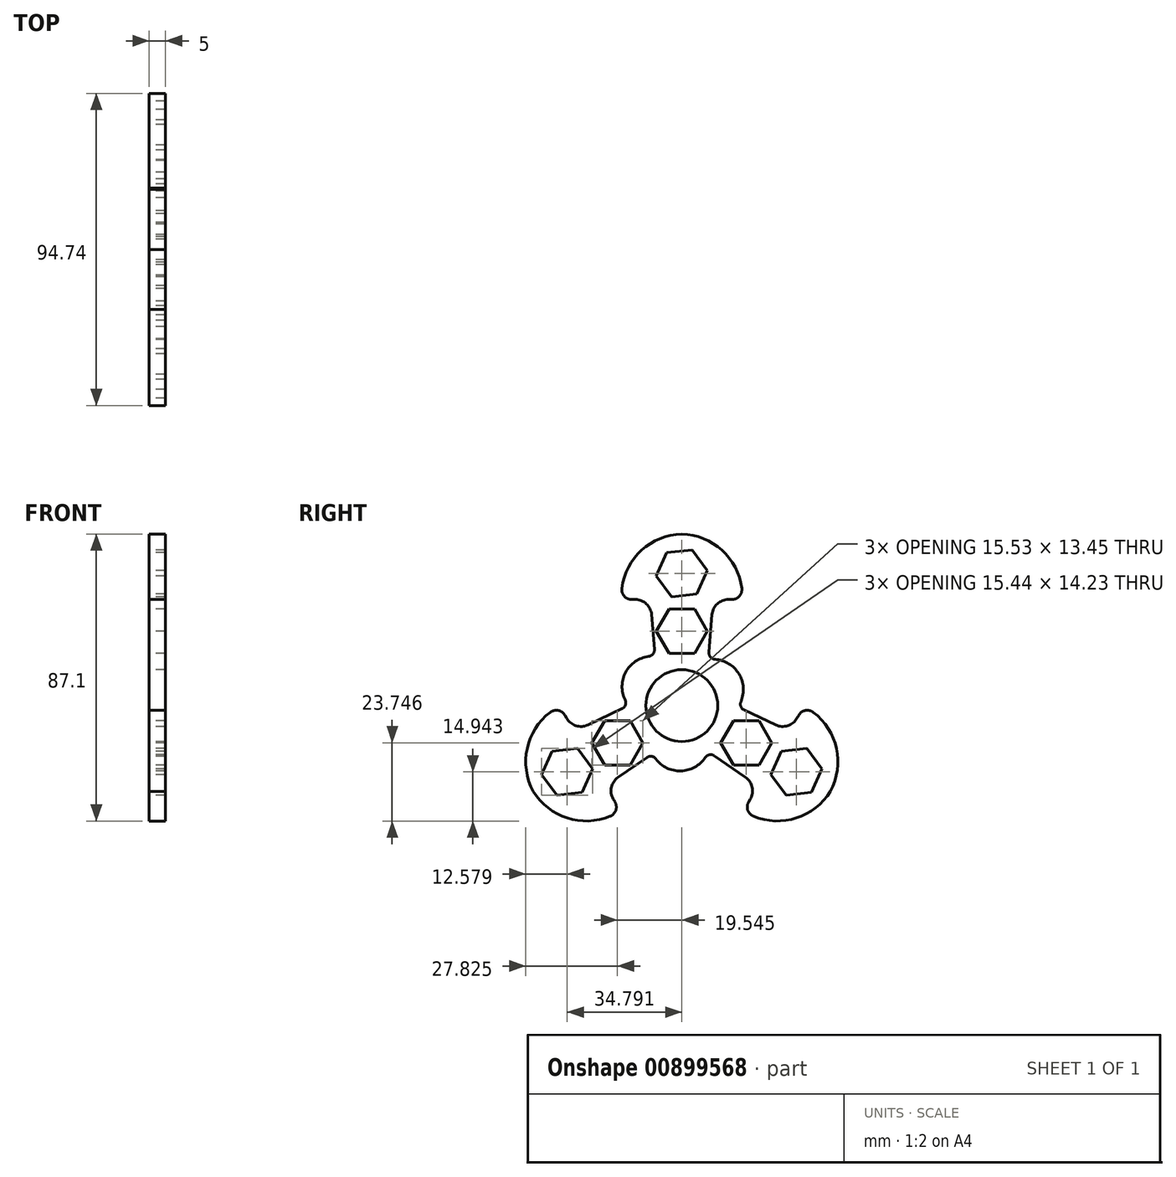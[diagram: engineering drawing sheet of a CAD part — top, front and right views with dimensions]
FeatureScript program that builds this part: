
annotation { "Feature Type Name" : "Feature", "Feature Type Description" : "" }
export const myFeature = defineFeature(function(context is Context, id is Id, definition is map)
    precondition{}
    {
        {
            var Q0;
            Q0=qCreatedBy(makeId("Right.planeOp"),FACE);
            var sketch = newSketch(context, id + "F0", { "sketchPlane" : qUnion([Q0])});
            skCircle(sketch, "E0", {"center": v(0, 0) * mm, "radius": 10.9 * mm});
            skCircle(sketch, "E1.cCircle", {"center": v(0, 22.57) * mm, "radius": 6.72 * mm, "construction": true});
            skLineSegment(sketch, "E1.0", {"start": v(-3.88, 29.3) * mm, "end": v(3.88, 29.3) * mm});
            skLineSegment(sketch, "E1.1", {"start": v(3.88, 29.3) * mm, "end": v(7.77, 22.57) * mm});
            skLineSegment(sketch, "E1.2", {"start": v(7.77, 22.57) * mm, "end": v(3.88, 15.84) * mm});
            skLineSegment(sketch, "E1.3", {"start": v(3.88, 15.84) * mm, "end": v(-3.88, 15.84) * mm});
            skLineSegment(sketch, "E1.4", {"start": v(-3.88, 15.84) * mm, "end": v(-7.77, 22.57) * mm});
            skLineSegment(sketch, "E1.5", {"start": v(-7.77, 22.57) * mm, "end": v(-3.88, 29.3) * mm});
            skPoint(sketch, "E1.0.midPoint", {"position": v(0, 29.3) * mm});
            skCircle(sketch, "E2.cCircle", {"center": v(0, 40.17) * mm, "radius": 6.72 * mm, "construction": true});
            skLineSegment(sketch, "E2.0", {"start": v(-7.72, 39.32) * mm, "end": v(-4.6, 46.43) * mm});
            skLineSegment(sketch, "E2.1", {"start": v(-4.6, 46.43) * mm, "end": v(3.12, 47.29) * mm});
            skLineSegment(sketch, "E2.2", {"start": v(3.12, 47.29) * mm, "end": v(7.72, 41.03) * mm});
            skLineSegment(sketch, "E2.3", {"start": v(7.72, 41.03) * mm, "end": v(4.6, 33.92) * mm});
            skLineSegment(sketch, "E2.4", {"start": v(4.6, 33.92) * mm, "end": v(-3.12, 33.06) * mm});
            skLineSegment(sketch, "E2.5", {"start": v(-3.12, 33.06) * mm, "end": v(-7.72, 39.32) * mm});
            skPoint(sketch, "E2.0.midPoint", {"position": v(-6.16, 42.87) * mm});
            skLineSegment(sketch, "E3", {"start": v(-8.3, 17.07) * mm, "end": v(-9.17, 27.6) * mm});
            skLineSegment(sketch, "E4.MirrorCS", {"start": v(8.24, 16.2) * mm, "end": v(9.17, 27.6) * mm});
            skLineSegment(sketch, "E5.1.0", {"start": v(-37.9, -27.2) * mm, "end": v(-42.5, -20.94) * mm});
            skLineSegment(sketch, "E5.1.1", {"start": v(-42.5, -20.94) * mm, "end": v(-39.4, -13.83) * mm});
            skLineSegment(sketch, "E5.1.2", {"start": v(-39.4, -13.83) * mm, "end": v(-31.68, -12.97) * mm});
            skCircle(sketch, "E5.1.3", {"center": v(-34.8, -20.09) * mm, "radius": 6.72 * mm, "construction": true});
            skLineSegment(sketch, "E5.1.4", {"start": v(-31.68, -12.97) * mm, "end": v(-27.07, -19.23) * mm});
            skLineSegment(sketch, "E5.1.5", {"start": v(-27.07, -19.23) * mm, "end": v(-30.19, -26.34) * mm});
            skLineSegment(sketch, "E5.1.6", {"start": v(-30.19, -26.34) * mm, "end": v(-37.9, -27.2) * mm});
            skLineSegment(sketch, "E5.1.7", {"start": v(-10.63, -15.73) * mm, "end": v(-19.32, -21.74) * mm});
            skLineSegment(sketch, "E5.1.10", {"start": v(-18.14, -0.96) * mm, "end": v(-28.5, -5.86) * mm});
            skLineSegment(sketch, "E5.1.11", {"start": v(-27.31, -11.28) * mm, "end": v(-23.43, -4.56) * mm});
            skCircle(sketch, "E5.1.12", {"center": v(-19.54, -11.28) * mm, "radius": 6.72 * mm, "construction": true});
            skLineSegment(sketch, "E5.1.13", {"start": v(-23.43, -4.56) * mm, "end": v(-15.66, -4.56) * mm});
            skLineSegment(sketch, "E5.1.14", {"start": v(-15.66, -4.56) * mm, "end": v(-11.78, -11.28) * mm});
            skLineSegment(sketch, "E5.1.15", {"start": v(-11.78, -11.28) * mm, "end": v(-15.66, -18) * mm});
            skLineSegment(sketch, "E5.1.16", {"start": v(-15.66, -18) * mm, "end": v(-23.43, -18) * mm});
            skLineSegment(sketch, "E5.1.17", {"start": v(-23.43, -18) * mm, "end": v(-27.31, -11.28) * mm});
            skLineSegment(sketch, "E5.2.0", {"start": v(42.5, -19.23) * mm, "end": v(39.4, -26.34) * mm});
            skLineSegment(sketch, "E5.2.1", {"start": v(39.4, -26.34) * mm, "end": v(31.68, -27.2) * mm});
            skLineSegment(sketch, "E5.2.2", {"start": v(31.68, -27.2) * mm, "end": v(27.07, -20.94) * mm});
            skCircle(sketch, "E5.2.3", {"center": v(34.8, -20.09) * mm, "radius": 6.72 * mm, "construction": true});
            skLineSegment(sketch, "E5.2.4", {"start": v(27.07, -20.94) * mm, "end": v(30.19, -13.83) * mm});
            skLineSegment(sketch, "E5.2.5", {"start": v(30.19, -13.83) * mm, "end": v(37.9, -12.97) * mm});
            skLineSegment(sketch, "E5.2.6", {"start": v(37.9, -12.97) * mm, "end": v(42.5, -19.23) * mm});
            skLineSegment(sketch, "E5.2.7", {"start": v(18.93, -1.34) * mm, "end": v(28.5, -5.86) * mm});
            skLineSegment(sketch, "E5.2.10", {"start": v(9.9, -15.23) * mm, "end": v(19.32, -21.74) * mm});
            skLineSegment(sketch, "E5.2.11", {"start": v(23.43, -18) * mm, "end": v(15.66, -18) * mm});
            skCircle(sketch, "E5.2.12", {"center": v(19.54, -11.28) * mm, "radius": 6.72 * mm, "construction": true});
            skLineSegment(sketch, "E5.2.13", {"start": v(15.66, -18) * mm, "end": v(11.78, -11.28) * mm});
            skLineSegment(sketch, "E5.2.14", {"start": v(11.78, -11.28) * mm, "end": v(15.66, -4.56) * mm});
            skLineSegment(sketch, "E5.2.15", {"start": v(15.66, -4.56) * mm, "end": v(23.43, -4.56) * mm});
            skLineSegment(sketch, "E5.2.16", {"start": v(23.43, -4.56) * mm, "end": v(27.31, -11.28) * mm});
            skLineSegment(sketch, "E5.2.17", {"start": v(27.31, -11.28) * mm, "end": v(23.43, -18) * mm});
            skLineSegment(sketch, "E6", {"start": v(-14.15, 32.2) * mm, "end": v(-15.23, 32.2) * mm});
            skArc(sketch, "E7", {"start": v(0, 52.07) * mm, "mid": v(-12.15, 47.19) * mm, "end": v(-18.2, 35.57) * mm});
            skArc(sketch, "E8.MirrorCS", {"start": v(0, 52.07) * mm, "mid": v(12.15, 47.19) * mm, "end": v(18.2, 35.57) * mm});
            skLineSegment(sketch, "E9.MirrorCS", {"start": v(14.15, 32.2) * mm, "end": v(15.23, 32.2) * mm});
            skLineSegment(sketch, "E10.1.0", {"start": v(-20.8, -28.35) * mm, "end": v(-20.27, -29.29) * mm});
            skArc(sketch, "E10.1.1", {"start": v(-45.1, -26.03) * mm, "mid": v(-34.79, -34.12) * mm, "end": v(-21.7, -33.55) * mm});
            skArc(sketch, "E10.1.2", {"start": v(-45.1, -26.03) * mm, "mid": v(-46.94, -13.07) * mm, "end": v(-39.91, -2.02) * mm});
            skLineSegment(sketch, "E10.1.3", {"start": v(-34.96, -3.84) * mm, "end": v(-35.5, -2.9) * mm});
            skLineSegment(sketch, "E10.2.0", {"start": v(34.96, -3.84) * mm, "end": v(35.5, -2.9) * mm});
            skArc(sketch, "E10.2.1", {"start": v(45.1, -26.03) * mm, "mid": v(46.94, -13.07) * mm, "end": v(39.91, -2.02) * mm});
            skArc(sketch, "E10.2.2", {"start": v(45.1, -26.03) * mm, "mid": v(34.79, -34.12) * mm, "end": v(21.7, -33.55) * mm});
            skLineSegment(sketch, "E10.2.3", {"start": v(20.8, -28.35) * mm, "end": v(20.27, -29.29) * mm});
            skArc(sketch, "E11", {"start": v(-10.06, 14.92) * mm, "mid": v(-17.03, 10.16) * mm, "end": v(-17.2, 1.72) * mm});
            skArc(sketch, "E12.1.0", {"start": v(-7.9, -16.17) * mm, "mid": v(-0.29, -19.83) * mm, "end": v(7.1, -15.76) * mm});
            skArc(sketch, "E12.2.0", {"start": v(17.95, 1.25) * mm, "mid": v(17.31, 9.67) * mm, "end": v(10.1, 14.03) * mm});
            skPoint(sketch, "E13.orphan", {"position": v(-7.55, 7.86) * mm});
            skPoint(sketch, "E14.visualSharp", {"position": v(-32.66, -7.83) * mm});
            skArc(sketch, "E14.filletArc", {"start": v(-34.96, -3.84) * mm, "mid": v(-32.12, -6.12) * mm, "end": v(-28.5, -5.86) * mm});
            skLineSegment(sketch, "E15.bottom", {"start": v(-55.43, 26.12) * mm, "end": v(-55.58, 26.12) * mm});
            skLineSegment(sketch, "E15.top", {"start": v(-55.43, 24.8) * mm, "end": v(-55.58, 24.8) * mm});
            skLineSegment(sketch, "E15.left", {"start": v(-55.43, 26.12) * mm, "end": v(-55.43, 24.8) * mm});
            skLineSegment(sketch, "E15.right", {"start": v(-55.58, 26.12) * mm, "end": v(-55.58, 24.8) * mm});
            skLineSegment(sketch, "E16.bottom", {"start": v(-68.95, 33.26) * mm, "end": v(-42.65, 33.26) * mm});
            skLineSegment(sketch, "E16.top", {"start": v(-67.95, 2.56) * mm, "end": v(-47.15, 2.56) * mm});
            skLineSegment(sketch, "E16.left", {"start": v(-70.95, 31.26) * mm, "end": v(-70.95, 5.56) * mm});
            skLineSegment(sketch, "E16.right", {"start": v(-42.15, 32.76) * mm, "end": v(-42.15, 7.56) * mm});
            skPoint(sketch, "E17.visualSharp", {"position": v(-42.15, 33.26) * mm});
            skArc(sketch, "E17.filletArc", {"start": v(-42.15, 32.76) * mm, "mid": v(-42.3, 33.11) * mm, "end": v(-42.65, 33.26) * mm});
            skPoint(sketch, "E18.visualSharp", {"position": v(-42.15, 2.56) * mm});
            skArc(sketch, "E18.filletArc", {"start": v(-47.15, 2.56) * mm, "mid": v(-43.61, 4.02) * mm, "end": v(-42.15, 7.56) * mm});
            skPoint(sketch, "E19.visualSharp", {"position": v(-70.95, 2.56) * mm});
            skArc(sketch, "E19.filletArc", {"start": v(-70.95, 5.56) * mm, "mid": v(-70.07, 3.44) * mm, "end": v(-67.95, 2.56) * mm});
            skPoint(sketch, "E20.visualSharp", {"position": v(-37.05, -0.22) * mm});
            skArc(sketch, "E20.filletArc", {"start": v(-35.5, -2.9) * mm, "mid": v(-37.5, -1.47) * mm, "end": v(-39.91, -2.02) * mm});
            skPoint(sketch, "E21.visualSharp", {"position": v(-18.72, -31.97) * mm});
            skArc(sketch, "E21.filletArc", {"start": v(-21.7, -33.55) * mm, "mid": v(-20.02, -31.75) * mm, "end": v(-20.27, -29.29) * mm});
            skPoint(sketch, "E22.visualSharp", {"position": v(-23.11, -24.36) * mm});
            skArc(sketch, "E22.filletArc", {"start": v(-19.32, -21.74) * mm, "mid": v(-21.36, -24.76) * mm, "end": v(-20.8, -28.35) * mm});
            skArc(sketch, "E23.1.1", {"start": v(20.27, -29.29) * mm, "mid": v(20.02, -31.75) * mm, "end": v(21.7, -33.55) * mm});
            skArc(sketch, "E23.1.3", {"start": v(39.91, -2.02) * mm, "mid": v(37.5, -1.47) * mm, "end": v(35.5, -2.9) * mm});
            skArc(sketch, "E23.2.1", {"start": v(15.23, 32.2) * mm, "mid": v(17.48, 33.21) * mm, "end": v(18.2, 35.57) * mm});
            skArc(sketch, "E23.2.3", {"start": v(-18.2, 35.57) * mm, "mid": v(-17.48, 33.21) * mm, "end": v(-15.23, 32.2) * mm});
            skPoint(sketch, "E24.orphan", {"position": v(37.05, -0.22) * mm});
            skPoint(sketch, "E25.orphan", {"position": v(18.72, -31.97) * mm});
            skPoint(sketch, "E26.orphan", {"position": v(18.33, 32.2) * mm});
            skPoint(sketch, "E27.orphan", {"position": v(-10.58, 2.61) * mm});
            skPoint(sketch, "E28.orphan", {"position": v(7.55, 7.86) * mm});
            skPoint(sketch, "E29.orphan", {"position": v(10.58, 2.61) * mm});
            skPoint(sketch, "E30.orphan", {"position": v(3.03, -10.47) * mm});
            skPoint(sketch, "E31.orphan", {"position": v(-3.03, -10.47) * mm});
            skPoint(sketch, "E32.visualSharp", {"position": v(-70.95, 33.26) * mm});
            skArc(sketch, "E32.filletArc", {"start": v(-68.95, 33.26) * mm, "mid": v(-70.37, 32.67) * mm, "end": v(-70.95, 31.26) * mm});
            skPoint(sketch, "E33.visualSharp", {"position": v(-16.1, 0) * mm});
            skArc(sketch, "E33.filletArc", {"start": v(-18.14, -0.96) * mm, "mid": v(-17.1, 0.18) * mm, "end": v(-17.2, 1.72) * mm});
            skPoint(sketch, "E34.visualSharp", {"position": v(-8.13, 14.95) * mm});
            skArc(sketch, "E34.filletArc", {"start": v(-10.06, 14.92) * mm, "mid": v(-8.75, 15.64) * mm, "end": v(-8.3, 17.07) * mm});
            skPoint(sketch, "E35.visualSharp", {"position": v(17.02, -0.43) * mm});
            skArc(sketch, "E35.filletArc", {"start": v(17.95, 1.25) * mm, "mid": v(17.92, -0.24) * mm, "end": v(18.93, -1.34) * mm});
            skPoint(sketch, "E36.visualSharp", {"position": v(8.05, 13.95) * mm});
            skArc(sketch, "E36.filletArc", {"start": v(8.24, 16.2) * mm, "mid": v(8.71, 14.72) * mm, "end": v(10.1, 14.03) * mm});
            skPoint(sketch, "E37.visualSharp", {"position": v(8.05, -13.95) * mm});
            skArc(sketch, "E37.filletArc", {"start": v(9.9, -15.23) * mm, "mid": v(8.4, -14.9) * mm, "end": v(7.1, -15.76) * mm});
            skPoint(sketch, "E38.visualSharp", {"position": v(-8.88, -14.52) * mm});
            skArc(sketch, "E38.filletArc", {"start": v(-7.9, -16.17) * mm, "mid": v(-9.17, -15.4) * mm, "end": v(-10.63, -15.73) * mm});
            skPoint(sketch, "E39.visualSharp", {"position": v(-9.54, 32.2) * mm});
            skArc(sketch, "E39.filletArc", {"start": v(-9.17, 27.6) * mm, "mid": v(-10.76, 30.87) * mm, "end": v(-14.15, 32.2) * mm});
            skPoint(sketch, "E40.visualSharp", {"position": v(9.54, 32.2) * mm});
            skArc(sketch, "E40.filletArc", {"start": v(14.15, 32.2) * mm, "mid": v(10.76, 30.87) * mm, "end": v(9.17, 27.6) * mm});
            skPoint(sketch, "E41.visualSharp", {"position": v(32.66, -7.83) * mm});
            skArc(sketch, "E41.filletArc", {"start": v(28.5, -5.86) * mm, "mid": v(32.12, -6.12) * mm, "end": v(34.96, -3.84) * mm});
            skPoint(sketch, "E42.visualSharp", {"position": v(23.11, -24.36) * mm});
            skArc(sketch, "E42.filletArc", {"start": v(20.8, -28.35) * mm, "mid": v(21.36, -24.76) * mm, "end": v(19.32, -21.74) * mm});
            skSolve(sketch);
        }
        {
            var Q0;
            Q0=makeQuery(id+"F0.imprint","IMPRINT",FACE,{"disambiguationData":[TD([[makeQuery(id+"F0.imprint","IMPRINT",EDGE,{"derivedFrom":sQuery(id+"F0.wireOp",EDGE,"E0")}),-1.0]])]});
            extrude(context, id + "F1", {"entities" : qUnion([Q0]), "depth" : 5 * mm, "offsetDistance" : 25 * mm});
        }
    });
